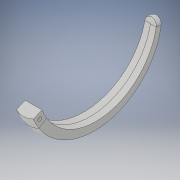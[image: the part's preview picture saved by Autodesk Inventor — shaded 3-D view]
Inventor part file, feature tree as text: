
AUTODESK INVENTOR PART (.ipt)
format: ipt  version: 2019 (Build 230136000, 136)  size: 523,264 bytes
history: native  units: mm
features: sketch x4, other x3, projected_geometry x2, plane x1, sweep x1, hole x1, revolve x1
ambient origin geometry x8: Origin, YZ Plane, XZ Plane, XY Plane, X Axis, Y Axis, Z Axis, Center Point
bodies: Body1 (feature_tree)
feature tree (13):
  other  "<userpath>\Desktop\3D Sketches\Bulova\Parameter.xlsx"
  other  "Foto"
  sketch  "Skizze15"  dims[d13=5.0mm d14=8.0mm d107=5.0mm d134=5.0mm]
  plane  "Arbeitsebene22"
  sweep  "Sweeping2"
  hole  "Bohrung1"  [1 undecoded]
  revolve  "Umdrehung1"
  other  "Bild1"
  sketch  "Skizze16"  dims[d140=4.5mm d141=2.5mm]
  sketch  "Skizze17"  dims[d142=-0.174533mm d143=0.0mm]
  projected_geometry  "Projizierte Kontur2"
  sketch  "Skizze18"  dims[d144=1.0mm d145=6.0mm d146=4.0mm d147=2.0mm d148=90.0deg d149=6.0mm d150=0.0mm d151=1.5mm d152=3.0mm d153=180.0deg d154=16.5mm]
  projected_geometry  "Projizierte Kontur3"
note: 1 required parameter value undecoded (feature->parameter linkage not recoverable at this tier; creation-order binding heuristic only, values carry confidence <= 0.55)
